# Revit family: RN 85143 Optiflex-Profix-Té
name_source: partatom
category: Rohrformteile
units: mm (PartAtom-declared; Revit-internal decimal feet)

## family parameters
Arbeitsebenenbasiert = Nein
Beim Laden mit Abzugskörper schneiden = Nein
Bemaßung runder Anschluss = Durchmesser verwenden
Gemeinsam genutzt = Nein
Immer vertikal = Ja
Teiletyp = T-Stück

## types (4) — shared parameters
1.010.00.2 Blattnummer der Richtlinie = 29
1.010.00.3 Ausgabedatum (Monat) der Richtlinie = 201308
1.010.00.4 Herstellername = R. Nussbaum AG
1.010.00.5 Revisionsdatum der Datei = 20190521
1.010.00.6 Webadresse des Herstellers = http://www.nussbaum.ch
1.100.00.4 Produktbezeichnung = Versorgung
1.110.00.2 Index = 5
1.110.00.4 Produktbezeichnung = Optiflex
1.960/3L.00.8 Link (URL) = https://www.nussbaum.ch
29.700.00.4 Produktname = Optiflex-Profix-T-Stück, mit Innengewinde
29.700.00.5 Produktkennung = 2
29.700.00.6 Querschnittsform = 1
29.700.00.7 Nennweitensystem = DN
29.700.00.8 Nenndrucksystem = PN
29.710.02.4 Nenndruck = 10
29.710.02.5 max. zul. Überdruck [hPa] = 1000
29.710.02.7 max. zul. Dauer-Betriebsdruck [hPa] = 1000
29.710.02.9 max. zul. Dauer-Betriebstemperatur [°C] = 70
Connector Visibility = Nein
EnclosingSpace Visibility = Nein
Hersteller = R. Nussbaum AG
URL = https://www.nussbaum.ch

## per-type parameters (varying)
- DN=20: 1.800.00.3 TGA-Nummer=01900500000000000000000000000000000000000000000092000000000000000004; 1.800.00.4 Kommentarfeld=85143.24, Optiflex-Profix-T-Stück, mit Innengewinde, DN=20, L=128, Rp=¾; 1.810.00.3 Hersteller-Bestellnummer=85143.24; 1.810.00.4 DATANORM-Nummer=85143.24; 1.810.00.6 GTIN-Nummer=7612945818515; 29.710.02.10 Formstück-Gewicht [kg]=0.341; 29.710.02.3 Benennung=Optiflex-Profix-T-Stück, mit Innengewinde, DN=20, L=128, Rp=¾; CONNECTOR0_DIAMETER_dX_0r=20 mm  [stored 0.0656168 ft]; CONNECTOR0_dX_00=22 mm  [stored 0.0721785 ft]; CONNECTOR0_dX_01=64 mm; CONNECTOR0_ref_dX=22 mm  [stored 0.0721785 ft]; CONNECTOR1_DIAMETER_dX_0r=20 mm  [stored 0.0656168 ft]; CONNECTOR1_dX_00=64 mm; CONNECTOR1_dX_01=22 mm  [stored 0.0721785 ft]; CONNECTOR1_ref_dX=22 mm  [stored 0.0721785 ft]; CONNECTOR2_DIAMETER_dY_0r=20 mm  [stored 0.0656168 ft]; CONNECTOR2_dY_00=35 mm; CONNECTOR2_dY_01=20 mm  [stored 0.0656168 ft]; CONNECTOR2_ref_dY=20 mm  [stored 0.0656168 ft]; Modell=85143.24; R. Nussbaum AG 85143.21 de Visibility=Nein; R. Nussbaum AG 85143.22 de Visibility=Nein; R. Nussbaum AG 85143.23 de Visibility=Nein; R. Nussbaum AG 85143.24 de Visibility=Ja; Typenkommentare=Optiflex-Profix-Té  DN=20
- DN=20x15x20: 1.800.00.3 TGA-Nummer=01900500000000000000000000000000000000000000000092000000000000000003; 1.800.00.4 Kommentarfeld=85143.23, Optiflex-Profix-T-Stück, mit Innengewinde, DN=20x15x20, L=128, Rp=½; 1.810.00.3 Hersteller-Bestellnummer=85143.23; 1.810.00.4 DATANORM-Nummer=85143.23; 1.810.00.6 GTIN-Nummer=7612945818508; 29.710.02.10 Formstück-Gewicht [kg]=0.319; 29.710.02.3 Benennung=Optiflex-Profix-T-Stück, mit Innengewinde, DN=20x15x20, L=128, Rp=½; CONNECTOR0_DIAMETER_dX_0r=20 mm  [stored 0.0656168 ft]; CONNECTOR0_dX_00=22 mm  [stored 0.0721785 ft]; CONNECTOR0_dX_01=64 mm; CONNECTOR0_ref_dX=22 mm  [stored 0.0721785 ft]; CONNECTOR1_DIAMETER_dX_0r=20 mm  [stored 0.0656168 ft]; CONNECTOR1_dX_00=64 mm; CONNECTOR1_dX_01=22 mm  [stored 0.0721785 ft]; CONNECTOR1_ref_dX=22 mm  [stored 0.0721785 ft]; CONNECTOR2_DIAMETER_dY_0r=15 mm; CONNECTOR2_dY_00=35 mm; CONNECTOR2_dY_01=22 mm  [stored 0.0721785 ft]; CONNECTOR2_ref_dY=22 mm  [stored 0.0721785 ft]; Modell=85143.23; R. Nussbaum AG 85143.21 de Visibility=Nein; R. Nussbaum AG 85143.22 de Visibility=Nein; R. Nussbaum AG 85143.23 de Visibility=Ja; R. Nussbaum AG 85143.24 de Visibility=Nein; Typenkommentare=Optiflex-Profix-Té  DN=20x15x20
- DN=15: 1.800.00.3 TGA-Nummer=01900500000000000000000000000000000000000000000092000000000000000002; 1.800.00.4 Kommentarfeld=85143.22, Optiflex-Profix-T-Stück, mit Innengewinde, DN=15, L=108, Rp=½; 1.810.00.3 Hersteller-Bestellnummer=85143.22; 1.810.00.4 DATANORM-Nummer=85143.22; 1.810.00.6 GTIN-Nummer=7612945818492; 29.710.02.10 Formstück-Gewicht [kg]=0.199; 29.710.02.3 Benennung=Optiflex-Profix-T-Stück, mit Innengewinde, DN=15, L=108, Rp=½; CONNECTOR0_DIAMETER_dX_0r=15 mm; CONNECTOR0_dX_00=20 mm  [stored 0.0656168 ft]; CONNECTOR0_dX_01=54 mm; CONNECTOR0_ref_dX=20 mm  [stored 0.0656168 ft]; CONNECTOR1_DIAMETER_dX_0r=15 mm; CONNECTOR1_dX_00=54 mm; CONNECTOR1_dX_01=20 mm  [stored 0.0656168 ft]; CONNECTOR1_ref_dX=20 mm  [stored 0.0656168 ft]; CONNECTOR2_DIAMETER_dY_0r=15 mm; CONNECTOR2_dY_00=33 mm; CONNECTOR2_dY_01=20 mm  [stored 0.0656168 ft]; CONNECTOR2_ref_dY=20 mm  [stored 0.0656168 ft]; Modell=85143.22; R. Nussbaum AG 85143.21 de Visibility=Nein; R. Nussbaum AG 85143.22 de Visibility=Ja; R. Nussbaum AG 85143.23 de Visibility=Nein; R. Nussbaum AG 85143.24 de Visibility=Nein; Typenkommentare=Optiflex-Profix-Té  DN=15
- DN=12x15x12: 1.800.00.3 TGA-Nummer=01900500000000000000000000000000000000000000000092000000000000000001; 1.800.00.4 Kommentarfeld=85143.21, Optiflex-Profix-T-Stück, mit Innengewinde, DN=12x15x12, L=104, Rp=½; 1.810.00.3 Hersteller-Bestellnummer=85143.21; 1.810.00.4 DATANORM-Nummer=85143.21; 1.810.00.6 GTIN-Nummer=7612945818485; 29.710.02.10 Formstück-Gewicht [kg]=0.17; 29.710.02.3 Benennung=Optiflex-Profix-T-Stück, mit Innengewinde, DN=12x15x12, L=104, Rp=½; CONNECTOR0_DIAMETER_dX_0r=12 mm  [stored 0.0393701 ft]; CONNECTOR0_dX_00=18 mm  [stored 0.0590551 ft]; CONNECTOR0_dX_01=52 mm; CONNECTOR0_ref_dX=18 mm  [stored 0.0590551 ft]; CONNECTOR1_DIAMETER_dX_0r=12 mm  [stored 0.0393701 ft]; CONNECTOR1_dX_00=52 mm; CONNECTOR1_dX_01=18 mm  [stored 0.0590551 ft]; CONNECTOR1_ref_dX=18 mm  [stored 0.0590551 ft]; CONNECTOR2_DIAMETER_dY_0r=15 mm; CONNECTOR2_dY_00=31 mm; CONNECTOR2_dY_01=18 mm  [stored 0.0590551 ft]; CONNECTOR2_ref_dY=18 mm  [stored 0.0590551 ft]; Modell=85143.21; R. Nussbaum AG 85143.21 de Visibility=Ja; R. Nussbaum AG 85143.22 de Visibility=Nein; R. Nussbaum AG 85143.23 de Visibility=Nein; R. Nussbaum AG 85143.24 de Visibility=Nein; Typenkommentare=Optiflex-Profix-Té  DN=12x15x12

note: [stored X ft] marks values corroborated as IEEE doubles in the binary element streams (Revit-internal decimal feet)

## geometry (parser evidence)
native form markers: Sweep x1
no freeform markers — native parametric forms only
